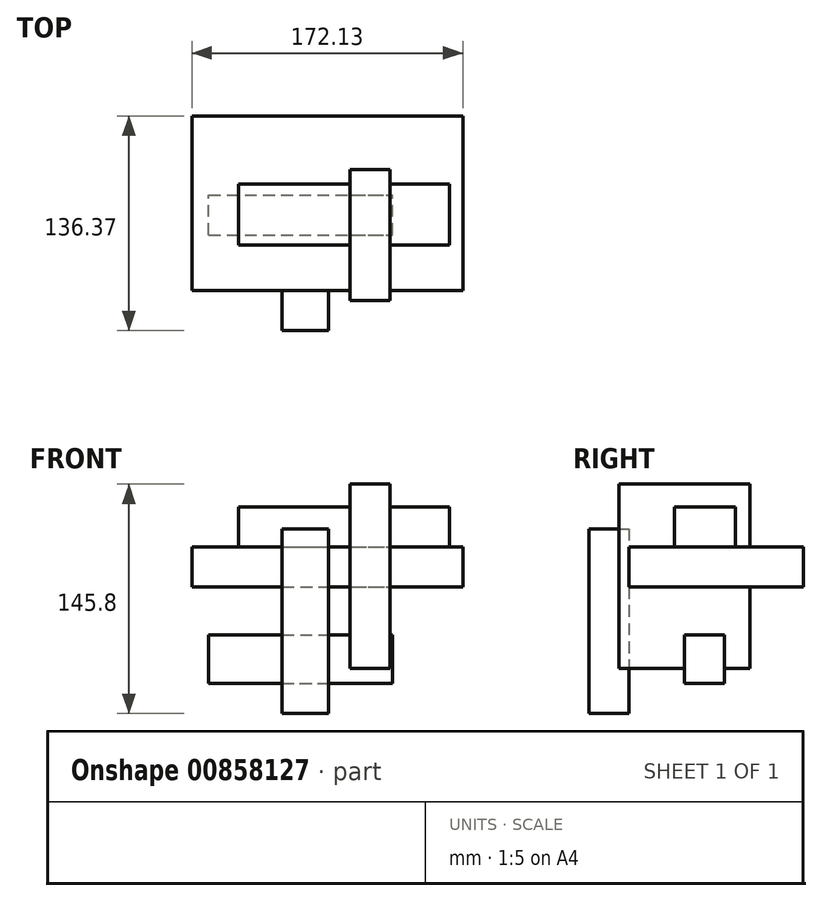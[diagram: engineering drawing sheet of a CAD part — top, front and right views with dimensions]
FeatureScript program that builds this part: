
annotation { "Feature Type Name" : "Feature", "Feature Type Description" : "" }
export const myFeature = defineFeature(function(context is Context, id is Id, definition is map)
    precondition{}
    {
        {
            var Q0;
            Q0=qCreatedBy(makeId("Right.planeOp"),FACE);
            var sketch = newSketch(context, id + "F0", { "sketchPlane" : qUnion([Q0])});
            skLineSegment(sketch, "E0.bottom", {"start": v(-66.96, 65.42) * mm, "end": v(16.22, 65.42) * mm});
            skLineSegment(sketch, "E0.top", {"start": v(-66.96, -51.57) * mm, "end": v(16.22, -51.57) * mm});
            skLineSegment(sketch, "E0.left", {"start": v(-66.96, 65.42) * mm, "end": v(-66.96, -51.57) * mm});
            skLineSegment(sketch, "E0.right", {"start": v(16.22, 65.42) * mm, "end": v(16.22, -51.57) * mm});
            skSolve(sketch);
        }
        {
            var Q0;
            Q0 = qSketchRegion(id + "F0", true);
            extrude(context, id + "F1", {"entities" : qUnion([Q0]), "depth" : 25.4 * mm, "offsetDistance" : 25.4 * mm});
        }
        {
            var Q0;
            Q0=qCreatedBy(makeId("Top.planeOp"),FACE);
            var sketch = newSketch(context, id + "F2", { "sketchPlane" : qUnion([Q0])});
            skLineSegment(sketch, "E1.bottom", {"start": v(-100.28, 50.16) * mm, "end": v(71.85, 50.16) * mm});
            skLineSegment(sketch, "E1.top", {"start": v(-100.28, -60.81) * mm, "end": v(71.85, -60.81) * mm});
            skLineSegment(sketch, "E1.left", {"start": v(-100.28, 50.16) * mm, "end": v(-100.28, -60.81) * mm});
            skLineSegment(sketch, "E1.right", {"start": v(71.85, 50.16) * mm, "end": v(71.85, -60.81) * mm});
            skSolve(sketch);
        }
        {
            var Q0;
            Q0 = qSketchRegion(id + "F2", true);
            extrude(context, id + "F3", {"entities" : qUnion([Q0]), "operationType" : NewBodyOperationType.ADD, "depth" : 25.4 * mm, "offsetDistance" : 25.4 * mm});
        }
        {
            var Q0;
            Q0=qCreatedBy(makeId("Front.planeOp"),FACE);
            var sketch = newSketch(context, id + "F4", { "sketchPlane" : qUnion([Q0])});
            skLineSegment(sketch, "E2.bottom", {"start": v(-89.57, -30.42) * mm, "end": v(27.13, -30.42) * mm});
            skLineSegment(sketch, "E2.top", {"start": v(-89.57, -61.08) * mm, "end": v(27.13, -61.08) * mm});
            skLineSegment(sketch, "E2.left", {"start": v(-89.57, -30.42) * mm, "end": v(-89.57, -61.08) * mm});
            skLineSegment(sketch, "E2.right", {"start": v(27.13, -30.42) * mm, "end": v(27.13, -61.08) * mm});
            skSolve(sketch);
        }
        {
            var Q0;
            Q0 = qSketchRegion(id + "F4", true);
            extrude(context, id + "F5", {"entities" : qUnion([Q0]), "operationType" : NewBodyOperationType.ADD, "depth" : 25.4 * mm, "offsetDistance" : 25.4 * mm});
        }
        {
            var Q0;
            Q0=makeQuery(id+"F3.opExtrude","CAP_FACE",FACE,{"disambiguationData":[OSD([sQuery(id+"F2.wireOp",EDGE,"E1.bottom"),sQuery(id+"F2.wireOp",EDGE,"E1.top"),sQuery(id+"F2.wireOp",EDGE,"E1.left"),sQuery(id+"F2.wireOp",EDGE,"E1.right")])],"isStart":false});
            var sketch = newSketch(context, id + "F6", { "sketchPlane" : qUnion([Q0])});
            skLineSegment(sketch, "E3.bottom", {"start": v(-70.52, 6.94) * mm, "end": v(63.37, 6.94) * mm});
            skLineSegment(sketch, "E3.top", {"start": v(-70.52, -31.98) * mm, "end": v(63.37, -31.98) * mm});
            skLineSegment(sketch, "E3.left", {"start": v(-70.52, 6.94) * mm, "end": v(-70.52, -31.98) * mm});
            skLineSegment(sketch, "E3.right", {"start": v(63.37, 6.94) * mm, "end": v(63.37, -31.98) * mm});
            skSolve(sketch);
        }
        {
            var Q0;
            Q0 = qSketchRegion(id + "F6", true);
            extrude(context, id + "F7", {"entities" : qUnion([Q0]), "operationType" : NewBodyOperationType.ADD, "depth" : 25.4 * mm, "offsetDistance" : 25.4 * mm});
        }
        {
            var Q0;
            {var subQ1=sQuery(id+"F2.wireOp",EDGE,"E1.left");var subQ2=sQuery(id+"F2.wireOp",EDGE,"E1.top");Q0=makeQuery(id+"F3.boolean.opBoolean","SPLIT",FACE,{"disambiguationData":[TD([makeQuery(id+"F3.opExtrude","SWEPT_FACE",FACE,{"disambiguationData":[OSD([subQ1])]})])],"derivedFrom":makeQuery(id+"F3.opExtrude","SWEPT_FACE",FACE,{"disambiguationData":[OSD([subQ2])]})});}
            var sketch = newSketch(context, id + "F8", { "sketchPlane" : qUnion([Q0])});
            skLineSegment(sketch, "E4.bottom", {"start": v(-42.93, 36.98) * mm, "end": v(-13.64, 36.98) * mm});
            skLineSegment(sketch, "E4.top", {"start": v(-42.93, -80.38) * mm, "end": v(-13.64, -80.38) * mm});
            skLineSegment(sketch, "E4.left", {"start": v(-42.93, 36.98) * mm, "end": v(-42.93, -80.38) * mm});
            skLineSegment(sketch, "E4.right", {"start": v(-13.64, 36.98) * mm, "end": v(-13.64, -80.38) * mm});
            skSolve(sketch);
        }
        {
            var Q0;
            Q0 = qSketchRegion(id + "F8", true);
            extrude(context, id + "F9", {"entities" : qUnion([Q0]), "operationType" : NewBodyOperationType.ADD, "depth" : 25.4 * mm, "offsetDistance" : 25.4 * mm});
        }
    });
